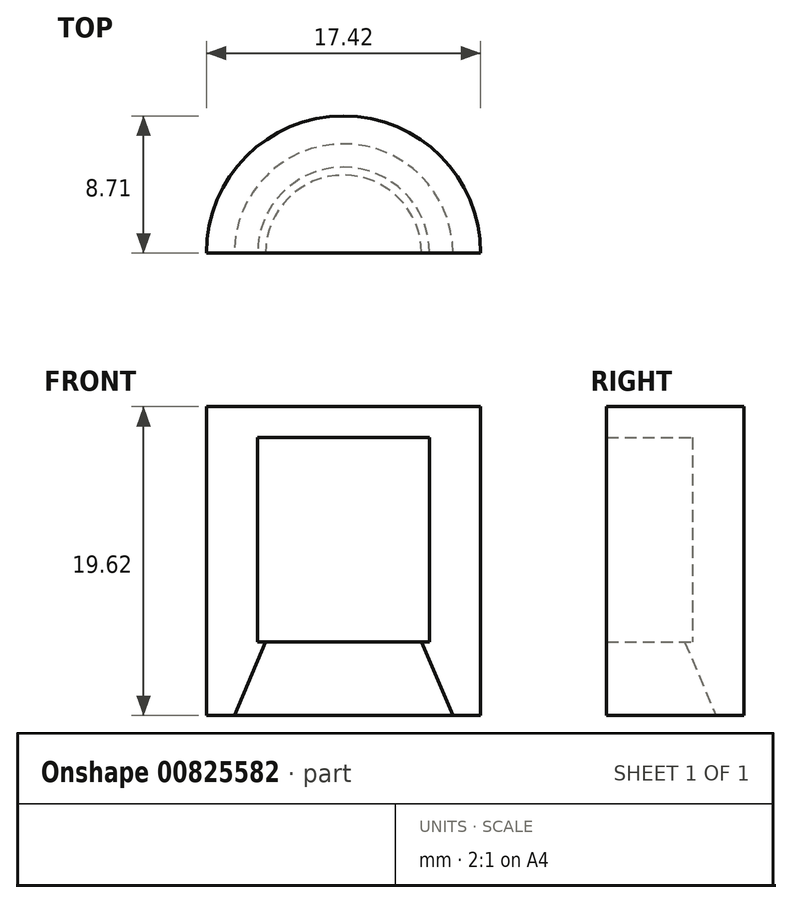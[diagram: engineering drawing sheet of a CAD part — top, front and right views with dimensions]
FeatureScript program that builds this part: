
annotation { "Feature Type Name" : "Feature", "Feature Type Description" : "" }
export const myFeature = defineFeature(function(context is Context, id is Id, definition is map)
    precondition{}
    {
        {
            var Q0;
            Q0=qCreatedBy(makeId("Front.planeOp"),FACE);
            var sketch = newSketch(context, id + "F0", { "sketchPlane" : qUnion([Q0])});
            skLineSegment(sketch, "E0", {"start": v(0, 0) * mm, "end": v(4.95, 0) * mm, "construction": true});
            skLineSegment(sketch, "E1", {"start": v(4.95, 0) * mm, "end": v(6.94, -4.68) * mm});
            skLineSegment(sketch, "E2", {"start": v(6.94, -4.68) * mm, "end": v(6.94, 12.97) * mm});
            skLineSegment(sketch, "E3", {"start": v(4.95, 0) * mm, "end": v(5.46, 0) * mm});
            skLineSegment(sketch, "E4", {"start": v(5.46, 0) * mm, "end": v(5.46, 12.97) * mm});
            skLineSegment(sketch, "E5", {"start": v(5.46, 12.97) * mm, "end": v(6.94, 12.97) * mm});
            skLineSegment(sketch, "E6.bottom", {"start": v(6.94, -4.68) * mm, "end": v(8.71, -4.68) * mm});
            skLineSegment(sketch, "E6.top", {"start": v(6.94, 12.97) * mm, "end": v(8.71, 12.97) * mm});
            skLineSegment(sketch, "E6.right", {"start": v(8.71, -4.68) * mm, "end": v(8.71, 12.97) * mm});
            skLineSegment(sketch, "E7", {"start": v(0, 0) * mm, "end": v(0, 4.38) * mm, "construction": true});
            skLineSegment(sketch, "E8.bottom", {"start": v(8.71, 12.97) * mm, "end": v(0, 12.97) * mm});
            skLineSegment(sketch, "E8.top", {"start": v(8.71, 14.94) * mm, "end": v(0, 14.94) * mm});
            skLineSegment(sketch, "E8.left", {"start": v(8.71, 12.97) * mm, "end": v(8.71, 14.94) * mm});
            skLineSegment(sketch, "E8.right", {"start": v(0, 12.97) * mm, "end": v(0, 14.94) * mm});
            skSolve(sketch);
        }
        {
            var Q0;
            Q0 = qSketchRegion(id + "F0", true);
            var Q1;
            Q1=sQuery(id+"F0.wireOp",EDGE,"E7");
            revolve(context, id + "F1", {"surfaceOperationType" : NewSurfaceOperationType.NEW, "entities" : qUnion([Q0]), "axis" : qUnion([Q1]), "revolveType" : RevolveType.ONE_DIRECTION, "angle" : 180 * degree});
        }
    });
